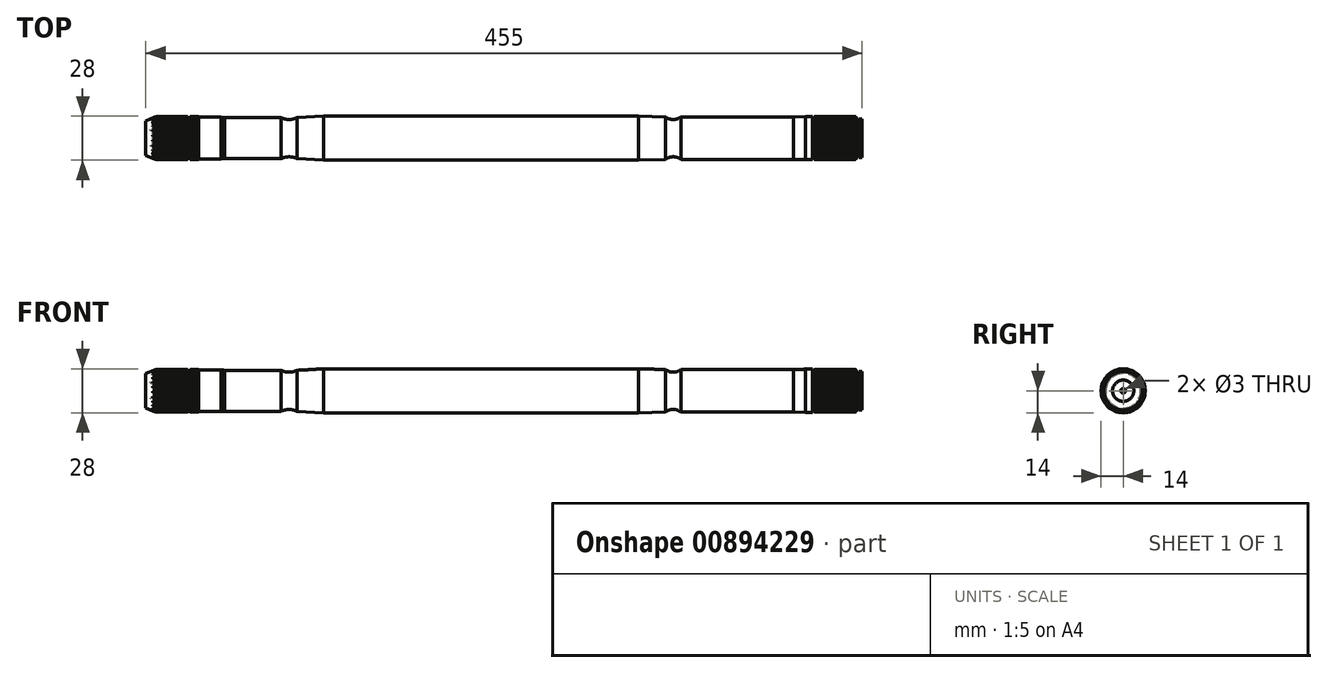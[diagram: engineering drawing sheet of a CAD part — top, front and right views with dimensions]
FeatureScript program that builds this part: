
annotation { "Feature Type Name" : "Feature", "Feature Type Description" : "" }
export const myFeature = defineFeature(function(context is Context, id is Id, definition is map)
    precondition{}
    {
        {
            var Q0;
            Q0=qCreatedBy(makeId("Front.planeOp"),FACE);
            var sketch = newSketch(context, id + "F0", { "sketchPlane" : qUnion([Q0])});
            skLineSegment(sketch, "E0", {"start": v(0, 6.75) * mm, "end": v(0, 12.2) * mm});
            skLineSegment(sketch, "E1.MirrorCS", {"start": v(-31, 12.75) * mm, "end": v(-31.5, 12.75) * mm});
            skLineSegment(sketch, "E2.MirrorCS", {"start": v(-31.5, 13.75) * mm, "end": v(-31.5, 12.75) * mm});
            skLineSegment(sketch, "E3.MirrorCS", {"start": v(-31, 12.75) * mm, "end": v(-30, 13.75) * mm});
            skLineSegment(sketch, "E4.MirrorCS", {"start": v(-31.5, 13.75) * mm, "end": v(-36, 13.75) * mm});
            skLineSegment(sketch, "E5.MirrorCS", {"start": v(-426.7, 13) * mm, "end": v(-428.5, 13) * mm});
            skLineSegment(sketch, "E6.MirrorCS", {"start": v(-421.5, 13.25) * mm, "end": v(-421.5, 13.75) * mm});
            skLineSegment(sketch, "E7.MirrorCS", {"start": v(-428.5, 13.75) * mm, "end": v(-428.5, 13) * mm});
            skLineSegment(sketch, "E8.MirrorCS", {"start": v(-426.7, 13.75) * mm, "end": v(-421.5, 13.75) * mm});
            skLineSegment(sketch, "E9.MirrorCS", {"start": v(-2, 12.2) * mm, "end": v(-2, 11.43) * mm});
            skLineSegment(sketch, "E10.MirrorCS", {"start": v(-426.7, 13.75) * mm, "end": v(-426.7, 13) * mm});
            skLineSegment(sketch, "E11.MirrorCS", {"start": v(-3.5, 11.43) * mm, "end": v(-3.5, 12.75) * mm});
            skLineSegment(sketch, "E12.MirrorCS", {"start": v(-4.5, 13.75) * mm, "end": v(-3.5, 12.75) * mm});
            skLineSegment(sketch, "E13.MirrorCS", {"start": v(0, 12.2) * mm, "end": v(-2, 12.2) * mm});
            skLineSegment(sketch, "E14.MirrorCS", {"start": v(-3.5, 11.43) * mm, "end": v(-2, 11.43) * mm});
            skLineSegment(sketch, "E15.MirrorCS", {"start": v(-443, 0) * mm, "end": v(-443.9, 1.5) * mm});
            skLineSegment(sketch, "E16.MirrorCS", {"start": v(-448, 13.75) * mm, "end": v(-455, 11) * mm});
            skLineSegment(sketch, "E17.MirrorCS", {"start": v(0, 6.75) * mm, "end": v(-9.1, 1.5) * mm});
            skLineSegment(sketch, "E18.MirrorCS", {"start": v(-405, 13) * mm, "end": v(-407, 13.25) * mm});
            skLineSegment(sketch, "E19.MirrorCS", {"start": v(-407, 13.25) * mm, "end": v(-421.5, 13.25) * mm});
            skArc(sketch, "E20.MirrorCS", {"start": v(-115, 13.5) * mm, "mid": v(-120, 11.85) * mm, "end": v(-125, 13.5) * mm});
            skLineSegment(sketch, "E21.MirrorCS", {"start": v(-455, 6.75) * mm, "end": v(-455, 11) * mm});
            skLineSegment(sketch, "E22.MirrorCS", {"start": v(-11.1, 1.5) * mm, "end": v(-9.1, 1.5) * mm});
            skLineSegment(sketch, "E23.MirrorCS", {"start": v(-455, 6.75) * mm, "end": v(-446, 1.5) * mm});
            skLineSegment(sketch, "E24.MirrorCS", {"start": v(-11.1, 1.5) * mm, "end": v(-12, 0) * mm});
            skArc(sketch, "E25.MirrorCS", {"start": v(-359, 13) * mm, "mid": v(-364, 11.85) * mm, "end": v(-369, 13) * mm});
            skLineSegment(sketch, "E26.MirrorCS", {"start": v(-36, 13.75) * mm, "end": v(-43.5, 13.5) * mm});
            skLineSegment(sketch, "E27.MirrorCS", {"start": v(-443.9, 1.5) * mm, "end": v(-446, 1.5) * mm});
            skLineSegment(sketch, "E28.MirrorCS", {"start": v(-428.5, 13.75) * mm, "end": v(-448, 13.75) * mm});
            skLineSegment(sketch, "E29.MirrorCS", {"start": v(-342, 14) * mm, "end": v(-359, 13) * mm});
            skLineSegment(sketch, "E30.MirrorCS", {"start": v(-443, 0) * mm, "end": v(-12, 0) * mm});
            skLineSegment(sketch, "E31.MirrorCS", {"start": v(-125, 13.5) * mm, "end": v(-142, 14) * mm});
            skLineSegment(sketch, "E32.MirrorCS", {"start": v(-369, 13) * mm, "end": v(-405, 13) * mm});
            skLineSegment(sketch, "E33.MirrorCS", {"start": v(-342, 14) * mm, "end": v(-142, 14) * mm});
            skLineSegment(sketch, "E34.MirrorCS", {"start": v(-43.5, 13.5) * mm, "end": v(-115, 13.5) * mm});
            skLineSegment(sketch, "E35.MirrorCS", {"start": v(-4.5, 13.75) * mm, "end": v(-30, 13.75) * mm});
            skSolve(sketch);
        }
        {
            var Q0;
            Q0=makeQuery(id+"F0.imprint","IMPRINT",FACE,{"disambiguationData":[TD([[makeQuery(id+"F0.imprint","IMPRINT",EDGE,{"derivedFrom":sQuery(id+"F0.wireOp",EDGE,"E0")}),1.0]])]});
            var Q1;
            Q1=sQuery(id+"F0.wireOp",EDGE,"E30.MirrorCS");
            revolve(context, id + "F1", {"surfaceOperationType" : NewSurfaceOperationType.NEW, "entities" : qUnion([Q0]), "axis" : qUnion([Q1]), "revolveType" : RevolveType.FULL});
        }
        {
            var Q0;
            Q0=qCreatedBy(makeId("Right.planeOp"),FACE);
            var sketch = newSketch(context, id + "F2", { "sketchPlane" : qUnion([Q0])});
            skArc(sketch, "E36", {"start": v(0.5, 13.56) * mm, "mid": v(0.25, 13.57) * mm, "end": v(0, 13.57) * mm});
            skArc(sketch, "E37", {"start": v(1.6, 12.57) * mm, "mid": v(1.47, 12.59) * mm, "end": v(1.34, 12.6) * mm});
            skLineSegment(sketch, "E38", {"start": v(1.34, 12.6) * mm, "end": v(0.5, 13.56) * mm});
            skArc(sketch, "E39", {"start": v(0, 13.57) * mm, "mid": v(-0.25, 13.57) * mm, "end": v(-0.5, 13.56) * mm});
            skArc(sketch, "E40", {"start": v(-1.34, 12.6) * mm, "mid": v(-1.47, 12.59) * mm, "end": v(-1.6, 12.57) * mm});
            skLineSegment(sketch, "E41", {"start": v(-1.34, 12.6) * mm, "end": v(-0.5, 13.56) * mm});
            skArc(sketch, "E42", {"start": v(-2.9, 13.26) * mm, "mid": v(-3.14, 13.2) * mm, "end": v(-3.38, 13.15) * mm});
            skArc(sketch, "E43", {"start": v(-1.6, 12.57) * mm, "mid": v(-1.72, 12.56) * mm, "end": v(-1.84, 12.54) * mm});
            skLineSegment(sketch, "E44", {"start": v(-1.84, 12.54) * mm, "end": v(-2.9, 13.26) * mm});
            skArc(sketch, "E45", {"start": v(-3.38, 13.15) * mm, "mid": v(-3.62, 13.08) * mm, "end": v(-3.86, 13.01) * mm});
            skArc(sketch, "E46", {"start": v(-4.44, 11.87) * mm, "mid": v(-4.56, 11.83) * mm, "end": v(-4.68, 11.78) * mm});
            skLineSegment(sketch, "E47", {"start": v(-4.44, 11.87) * mm, "end": v(-3.86, 13.01) * mm});
            skArc(sketch, "E48", {"start": v(-6.1, 12.12) * mm, "mid": v(-6.33, 12) * mm, "end": v(-6.55, 11.9) * mm});
            skArc(sketch, "E49", {"start": v(-4.68, 11.78) * mm, "mid": v(-4.8, 11.73) * mm, "end": v(-4.9, 11.69) * mm});
            skLineSegment(sketch, "E50", {"start": v(-4.9, 11.69) * mm, "end": v(-6.1, 12.12) * mm});
            skArc(sketch, "E51", {"start": v(-6.55, 11.9) * mm, "mid": v(-6.77, 11.77) * mm, "end": v(-6.99, 11.64) * mm});
            skArc(sketch, "E52", {"start": v(-7.26, 10.4) * mm, "mid": v(-7.36, 10.32) * mm, "end": v(-7.46, 10.25) * mm});
            skLineSegment(sketch, "E53", {"start": v(-7.26, 10.4) * mm, "end": v(-6.99, 11.64) * mm});
            skArc(sketch, "E54", {"start": v(-8.94, 10.22) * mm, "mid": v(-9.13, 10.06) * mm, "end": v(-9.3, 9.89) * mm});
            skArc(sketch, "E55", {"start": v(-7.46, 10.25) * mm, "mid": v(-7.57, 10.17) * mm, "end": v(-7.67, 10.1) * mm});
            skLineSegment(sketch, "E56", {"start": v(-7.67, 10.1) * mm, "end": v(-8.94, 10.22) * mm});
            skArc(sketch, "E57", {"start": v(-9.3, 9.89) * mm, "mid": v(-9.5, 9.71) * mm, "end": v(-9.67, 9.54) * mm});
            skArc(sketch, "E58", {"start": v(-9.62, 8.26) * mm, "mid": v(-9.7, 8.17) * mm, "end": v(-9.79, 8.07) * mm});
            skLineSegment(sketch, "E59", {"start": v(-9.62, 8.26) * mm, "end": v(-9.67, 9.54) * mm});
            skArc(sketch, "E60", {"start": v(-11.2, 7.68) * mm, "mid": v(-11.35, 7.47) * mm, "end": v(-11.48, 7.26) * mm});
            skArc(sketch, "E61", {"start": v(-9.79, 8.07) * mm, "mid": v(-9.87, 7.97) * mm, "end": v(-9.94, 7.87) * mm});
            skLineSegment(sketch, "E62", {"start": v(-9.94, 7.87) * mm, "end": v(-11.2, 7.68) * mm});
            skArc(sketch, "E63", {"start": v(-11.48, 7.26) * mm, "mid": v(-11.61, 7.05) * mm, "end": v(-11.74, 6.83) * mm});
            skArc(sketch, "E64", {"start": v(-11.38, 5.6) * mm, "mid": v(-11.44, 5.5) * mm, "end": v(-11.5, 5.38) * mm});
            skLineSegment(sketch, "E65", {"start": v(-11.38, 5.6) * mm, "end": v(-11.74, 6.83) * mm});
            skArc(sketch, "E66", {"start": v(-12.77, 4.65) * mm, "mid": v(-12.85, 4.41) * mm, "end": v(-12.93, 4.18) * mm});
            skArc(sketch, "E67", {"start": v(-11.5, 5.38) * mm, "mid": v(-11.54, 5.27) * mm, "end": v(-11.6, 5.15) * mm});
            skLineSegment(sketch, "E68", {"start": v(-11.6, 5.15) * mm, "end": v(-12.77, 4.65) * mm});
            skArc(sketch, "E69", {"start": v(-12.93, 4.18) * mm, "mid": v(-13, 3.94) * mm, "end": v(-13.08, 3.7) * mm});
            skArc(sketch, "E70", {"start": v(-12.43, 2.6) * mm, "mid": v(-12.45, 2.48) * mm, "end": v(-12.48, 2.35) * mm});
            skLineSegment(sketch, "E71", {"start": v(-12.43, 2.6) * mm, "end": v(-13.08, 3.7) * mm});
            skArc(sketch, "E72", {"start": v(-13.53, 1.33) * mm, "mid": v(-13.56, 1.08) * mm, "end": v(-13.57, 0.83) * mm});
            skArc(sketch, "E73", {"start": v(-12.48, 2.35) * mm, "mid": v(-12.5, 2.23) * mm, "end": v(-12.52, 2.1) * mm});
            skLineSegment(sketch, "E74", {"start": v(-12.52, 2.1) * mm, "end": v(-13.53, 1.33) * mm});
            skArc(sketch, "E75", {"start": v(-13.57, 0.83) * mm, "mid": v(-13.59, 0.58) * mm, "end": v(-13.6, 0.33) * mm});
            skArc(sketch, "E76", {"start": v(-12.69, -0.57) * mm, "mid": v(-12.68, -0.7) * mm, "end": v(-12.67, -0.82) * mm});
            skLineSegment(sketch, "E77", {"start": v(-12.69, -0.57) * mm, "end": v(-13.6, 0.33) * mm});
            skArc(sketch, "E78", {"start": v(-13.44, -2.08) * mm, "mid": v(-13.4, -2.33) * mm, "end": v(-13.36, -2.58) * mm});
            skArc(sketch, "E79", {"start": v(-12.67, -0.82) * mm, "mid": v(-12.67, -0.95) * mm, "end": v(-12.66, -1.08) * mm});
            skLineSegment(sketch, "E80", {"start": v(-12.66, -1.08) * mm, "end": v(-13.44, -2.08) * mm});
            skArc(sketch, "E81", {"start": v(-13.36, -2.58) * mm, "mid": v(-13.3, -2.82) * mm, "end": v(-13.26, -3.06) * mm});
            skArc(sketch, "E82", {"start": v(-12.15, -3.71) * mm, "mid": v(-12.12, -3.83) * mm, "end": v(-12.08, -3.95) * mm});
            skLineSegment(sketch, "E83", {"start": v(-12.15, -3.71) * mm, "end": v(-13.26, -3.06) * mm});
            skArc(sketch, "E84", {"start": v(-12.51, -5.36) * mm, "mid": v(-12.41, -5.6) * mm, "end": v(-12.3, -5.82) * mm});
            skArc(sketch, "E85", {"start": v(-12.08, -3.95) * mm, "mid": v(-12.04, -4.07) * mm, "end": v(-12, -4.2) * mm});
            skLineSegment(sketch, "E86", {"start": v(-12, -4.2) * mm, "end": v(-12.51, -5.36) * mm});
            skArc(sketch, "E87", {"start": v(-12.3, -5.82) * mm, "mid": v(-12.2, -6.04) * mm, "end": v(-12.08, -6.27) * mm});
            skArc(sketch, "E88", {"start": v(-10.86, -6.62) * mm, "mid": v(-10.79, -6.73) * mm, "end": v(-10.72, -6.83) * mm});
            skLineSegment(sketch, "E89", {"start": v(-10.86, -6.62) * mm, "end": v(-12.08, -6.27) * mm});
            skArc(sketch, "E90", {"start": v(-10.8, -8.3) * mm, "mid": v(-10.64, -8.5) * mm, "end": v(-10.48, -8.7) * mm});
            skArc(sketch, "E91", {"start": v(-10.72, -6.83) * mm, "mid": v(-10.65, -6.94) * mm, "end": v(-10.59, -7.04) * mm});
            skLineSegment(sketch, "E92", {"start": v(-10.59, -7.04) * mm, "end": v(-10.8, -8.3) * mm});
            skArc(sketch, "E93", {"start": v(-10.48, -8.7) * mm, "mid": v(-10.32, -8.89) * mm, "end": v(-10.15, -9.08) * mm});
            skArc(sketch, "E94", {"start": v(-8.88, -9.11) * mm, "mid": v(-8.79, -9.2) * mm, "end": v(-8.7, -9.28) * mm});
            skLineSegment(sketch, "E95", {"start": v(-8.88, -9.11) * mm, "end": v(-10.15, -9.08) * mm});
            skArc(sketch, "E96", {"start": v(-8.4, -10.73) * mm, "mid": v(-8.2, -10.88) * mm, "end": v(-8, -11.03) * mm});
            skArc(sketch, "E97", {"start": v(-8.7, -9.28) * mm, "mid": v(-8.6, -9.37) * mm, "end": v(-8.5, -9.46) * mm});
            skLineSegment(sketch, "E98", {"start": v(-8.5, -9.46) * mm, "end": v(-8.4, -10.73) * mm});
            skArc(sketch, "E99", {"start": v(-8, -11.03) * mm, "mid": v(-7.8, -11.17) * mm, "end": v(-7.58, -11.32) * mm});
            skArc(sketch, "E100", {"start": v(-6.34, -11.03) * mm, "mid": v(-6.23, -11.1) * mm, "end": v(-6.12, -11.16) * mm});
            skLineSegment(sketch, "E101", {"start": v(-6.34, -11.03) * mm, "end": v(-7.58, -11.32) * mm});
            skArc(sketch, "E102", {"start": v(-5.47, -12.48) * mm, "mid": v(-5.24, -12.58) * mm, "end": v(-5, -12.67) * mm});
            skArc(sketch, "E103", {"start": v(-6.12, -11.16) * mm, "mid": v(-6, -11.22) * mm, "end": v(-5.9, -11.28) * mm});
            skLineSegment(sketch, "E104", {"start": v(-5.9, -11.28) * mm, "end": v(-5.47, -12.48) * mm});
            skArc(sketch, "E105", {"start": v(-5, -12.67) * mm, "mid": v(-4.77, -12.76) * mm, "end": v(-4.54, -12.85) * mm});
            skArc(sketch, "E106", {"start": v(-3.4, -12.26) * mm, "mid": v(-3.28, -12.3) * mm, "end": v(-3.16, -12.33) * mm});
            skLineSegment(sketch, "E107", {"start": v(-3.4, -12.26) * mm, "end": v(-4.54, -12.85) * mm});
            skArc(sketch, "E108", {"start": v(-2.2, -13.45) * mm, "mid": v(-1.95, -13.49) * mm, "end": v(-1.7, -13.52) * mm});
            skArc(sketch, "E109", {"start": v(-3.16, -12.33) * mm, "mid": v(-3.04, -12.36) * mm, "end": v(-2.91, -12.39) * mm});
            skLineSegment(sketch, "E110", {"start": v(-2.91, -12.39) * mm, "end": v(-2.2, -13.45) * mm});
            skArc(sketch, "E111", {"start": v(-1.7, -13.52) * mm, "mid": v(-1.46, -13.55) * mm, "end": v(-1.2, -13.57) * mm});
            skArc(sketch, "E112", {"start": v(-0.25, -12.72) * mm, "mid": v(-0.13, -12.73) * mm, "end": v(0, -12.73) * mm});
            skLineSegment(sketch, "E113", {"start": v(-0.25, -12.72) * mm, "end": v(-1.2, -13.57) * mm});
            skArc(sketch, "E114", {"start": v(1.2, -13.57) * mm, "mid": v(1.46, -13.55) * mm, "end": v(1.7, -13.52) * mm});
            skArc(sketch, "E115", {"start": v(0, -12.73) * mm, "mid": v(0.13, -12.73) * mm, "end": v(0.25, -12.72) * mm});
            skLineSegment(sketch, "E116", {"start": v(0.25, -12.72) * mm, "end": v(1.2, -13.57) * mm});
            skArc(sketch, "E117", {"start": v(1.7, -13.52) * mm, "mid": v(1.95, -13.49) * mm, "end": v(2.2, -13.45) * mm});
            skArc(sketch, "E118", {"start": v(2.91, -12.39) * mm, "mid": v(3.04, -12.36) * mm, "end": v(3.16, -12.33) * mm});
            skLineSegment(sketch, "E119", {"start": v(2.91, -12.39) * mm, "end": v(2.2, -13.45) * mm});
            skArc(sketch, "E120", {"start": v(4.54, -12.85) * mm, "mid": v(4.77, -12.76) * mm, "end": v(5, -12.67) * mm});
            skArc(sketch, "E121", {"start": v(3.16, -12.33) * mm, "mid": v(3.28, -12.3) * mm, "end": v(3.4, -12.26) * mm});
            skLineSegment(sketch, "E122", {"start": v(3.4, -12.26) * mm, "end": v(4.54, -12.85) * mm});
            skArc(sketch, "E123", {"start": v(5, -12.67) * mm, "mid": v(5.24, -12.58) * mm, "end": v(5.47, -12.48) * mm});
            skArc(sketch, "E124", {"start": v(5.9, -11.28) * mm, "mid": v(6, -11.22) * mm, "end": v(6.12, -11.16) * mm});
            skLineSegment(sketch, "E125", {"start": v(5.9, -11.28) * mm, "end": v(5.47, -12.48) * mm});
            skArc(sketch, "E126", {"start": v(7.58, -11.32) * mm, "mid": v(7.8, -11.17) * mm, "end": v(8, -11.03) * mm});
            skArc(sketch, "E127", {"start": v(6.12, -11.16) * mm, "mid": v(6.23, -11.1) * mm, "end": v(6.34, -11.03) * mm});
            skLineSegment(sketch, "E128", {"start": v(6.34, -11.03) * mm, "end": v(7.58, -11.32) * mm});
            skArc(sketch, "E129", {"start": v(8, -11.03) * mm, "mid": v(8.2, -10.88) * mm, "end": v(8.4, -10.73) * mm});
            skArc(sketch, "E130", {"start": v(8.5, -9.46) * mm, "mid": v(8.6, -9.37) * mm, "end": v(8.7, -9.28) * mm});
            skLineSegment(sketch, "E131", {"start": v(8.5, -9.46) * mm, "end": v(8.4, -10.73) * mm});
            skArc(sketch, "E132", {"start": v(10.15, -9.08) * mm, "mid": v(10.32, -8.89) * mm, "end": v(10.48, -8.7) * mm});
            skArc(sketch, "E133", {"start": v(8.7, -9.28) * mm, "mid": v(8.79, -9.2) * mm, "end": v(8.88, -9.11) * mm});
            skLineSegment(sketch, "E134", {"start": v(8.88, -9.11) * mm, "end": v(10.15, -9.08) * mm});
            skArc(sketch, "E135", {"start": v(10.48, -8.7) * mm, "mid": v(10.64, -8.5) * mm, "end": v(10.8, -8.3) * mm});
            skArc(sketch, "E136", {"start": v(10.59, -7.04) * mm, "mid": v(10.65, -6.94) * mm, "end": v(10.72, -6.83) * mm});
            skLineSegment(sketch, "E137", {"start": v(10.59, -7.04) * mm, "end": v(10.8, -8.3) * mm});
            skArc(sketch, "E138", {"start": v(12.08, -6.27) * mm, "mid": v(12.2, -6.04) * mm, "end": v(12.3, -5.82) * mm});
            skArc(sketch, "E139", {"start": v(10.72, -6.83) * mm, "mid": v(10.79, -6.73) * mm, "end": v(10.86, -6.62) * mm});
            skLineSegment(sketch, "E140", {"start": v(10.86, -6.62) * mm, "end": v(12.08, -6.27) * mm});
            skArc(sketch, "E141", {"start": v(12.3, -5.82) * mm, "mid": v(12.41, -5.6) * mm, "end": v(12.51, -5.36) * mm});
            skArc(sketch, "E142", {"start": v(12, -4.2) * mm, "mid": v(12.04, -4.07) * mm, "end": v(12.08, -3.95) * mm});
            skLineSegment(sketch, "E143", {"start": v(12, -4.2) * mm, "end": v(12.51, -5.36) * mm});
            skArc(sketch, "E144", {"start": v(13.26, -3.06) * mm, "mid": v(13.3, -2.82) * mm, "end": v(13.36, -2.58) * mm});
            skArc(sketch, "E145", {"start": v(12.08, -3.95) * mm, "mid": v(12.12, -3.83) * mm, "end": v(12.15, -3.71) * mm});
            skLineSegment(sketch, "E146", {"start": v(12.15, -3.71) * mm, "end": v(13.26, -3.06) * mm});
            skArc(sketch, "E147", {"start": v(13.36, -2.58) * mm, "mid": v(13.4, -2.33) * mm, "end": v(13.44, -2.08) * mm});
            skArc(sketch, "E148", {"start": v(12.66, -1.08) * mm, "mid": v(12.67, -0.95) * mm, "end": v(12.67, -0.82) * mm});
            skLineSegment(sketch, "E149", {"start": v(12.66, -1.08) * mm, "end": v(13.44, -2.08) * mm});
            skArc(sketch, "E150", {"start": v(13.6, 0.33) * mm, "mid": v(13.59, 0.58) * mm, "end": v(13.57, 0.83) * mm});
            skArc(sketch, "E151", {"start": v(12.67, -0.82) * mm, "mid": v(12.68, -0.7) * mm, "end": v(12.69, -0.57) * mm});
            skLineSegment(sketch, "E152", {"start": v(12.69, -0.57) * mm, "end": v(13.6, 0.33) * mm});
            skArc(sketch, "E153", {"start": v(13.57, 0.83) * mm, "mid": v(13.56, 1.08) * mm, "end": v(13.53, 1.33) * mm});
            skArc(sketch, "E154", {"start": v(12.52, 2.1) * mm, "mid": v(12.5, 2.23) * mm, "end": v(12.48, 2.35) * mm});
            skLineSegment(sketch, "E155", {"start": v(12.52, 2.1) * mm, "end": v(13.53, 1.33) * mm});
            skArc(sketch, "E156", {"start": v(13.08, 3.7) * mm, "mid": v(13, 3.94) * mm, "end": v(12.93, 4.18) * mm});
            skArc(sketch, "E157", {"start": v(12.48, 2.35) * mm, "mid": v(12.45, 2.48) * mm, "end": v(12.43, 2.6) * mm});
            skLineSegment(sketch, "E158", {"start": v(12.43, 2.6) * mm, "end": v(13.08, 3.7) * mm});
            skArc(sketch, "E159", {"start": v(12.93, 4.18) * mm, "mid": v(12.85, 4.41) * mm, "end": v(12.77, 4.65) * mm});
            skArc(sketch, "E160", {"start": v(11.6, 5.15) * mm, "mid": v(11.54, 5.27) * mm, "end": v(11.5, 5.38) * mm});
            skLineSegment(sketch, "E161", {"start": v(11.6, 5.15) * mm, "end": v(12.77, 4.65) * mm});
            skArc(sketch, "E162", {"start": v(11.74, 6.83) * mm, "mid": v(11.61, 7.05) * mm, "end": v(11.48, 7.26) * mm});
            skArc(sketch, "E163", {"start": v(11.5, 5.38) * mm, "mid": v(11.44, 5.5) * mm, "end": v(11.38, 5.6) * mm});
            skLineSegment(sketch, "E164", {"start": v(11.38, 5.6) * mm, "end": v(11.74, 6.83) * mm});
            skArc(sketch, "E165", {"start": v(11.48, 7.26) * mm, "mid": v(11.35, 7.47) * mm, "end": v(11.2, 7.68) * mm});
            skArc(sketch, "E166", {"start": v(9.94, 7.87) * mm, "mid": v(9.87, 7.97) * mm, "end": v(9.79, 8.07) * mm});
            skLineSegment(sketch, "E167", {"start": v(9.94, 7.87) * mm, "end": v(11.2, 7.68) * mm});
            skArc(sketch, "E168", {"start": v(9.67, 9.54) * mm, "mid": v(9.5, 9.71) * mm, "end": v(9.3, 9.89) * mm});
            skArc(sketch, "E169", {"start": v(9.79, 8.07) * mm, "mid": v(9.7, 8.17) * mm, "end": v(9.62, 8.26) * mm});
            skLineSegment(sketch, "E170", {"start": v(9.62, 8.26) * mm, "end": v(9.67, 9.54) * mm});
            skArc(sketch, "E171", {"start": v(9.3, 9.89) * mm, "mid": v(9.13, 10.06) * mm, "end": v(8.94, 10.22) * mm});
            skArc(sketch, "E172", {"start": v(7.67, 10.1) * mm, "mid": v(7.57, 10.17) * mm, "end": v(7.46, 10.25) * mm});
            skLineSegment(sketch, "E173", {"start": v(7.67, 10.1) * mm, "end": v(8.94, 10.22) * mm});
            skArc(sketch, "E174", {"start": v(6.99, 11.64) * mm, "mid": v(6.77, 11.77) * mm, "end": v(6.55, 11.9) * mm});
            skArc(sketch, "E175", {"start": v(7.46, 10.25) * mm, "mid": v(7.36, 10.32) * mm, "end": v(7.26, 10.4) * mm});
            skLineSegment(sketch, "E176", {"start": v(7.26, 10.4) * mm, "end": v(6.99, 11.64) * mm});
            skArc(sketch, "E177", {"start": v(6.55, 11.9) * mm, "mid": v(6.33, 12) * mm, "end": v(6.1, 12.12) * mm});
            skArc(sketch, "E178", {"start": v(4.9, 11.69) * mm, "mid": v(4.8, 11.73) * mm, "end": v(4.68, 11.78) * mm});
            skLineSegment(sketch, "E179", {"start": v(4.9, 11.69) * mm, "end": v(6.1, 12.12) * mm});
            skArc(sketch, "E180", {"start": v(3.86, 13.01) * mm, "mid": v(3.62, 13.08) * mm, "end": v(3.38, 13.15) * mm});
            skArc(sketch, "E181", {"start": v(4.68, 11.78) * mm, "mid": v(4.56, 11.83) * mm, "end": v(4.44, 11.87) * mm});
            skLineSegment(sketch, "E182", {"start": v(4.44, 11.87) * mm, "end": v(3.86, 13.01) * mm});
            skArc(sketch, "E183", {"start": v(3.38, 13.15) * mm, "mid": v(3.14, 13.2) * mm, "end": v(2.9, 13.26) * mm});
            skArc(sketch, "E184", {"start": v(1.84, 12.54) * mm, "mid": v(1.72, 12.56) * mm, "end": v(1.6, 12.57) * mm});
            skLineSegment(sketch, "E185", {"start": v(1.84, 12.54) * mm, "end": v(2.9, 13.26) * mm});
            skCircle(sketch, "E186", {"center": v(0, 0) * mm, "radius": 14.27 * mm});
            skSolve(sketch);
        }
        {
            var Q0;
            Q0=qSketchRegion(id+"F2",true);
            var Q1;
            Q1=makeQuery(id+"F1.opRevolve","SWEPT_FACE",FACE,{"disambiguationData":[OSD([sQuery(id+"F0.wireOp",EDGE,"E3.MirrorCS")])]});
            extrude(context, id + "F3", {"entities" : qUnion([Q0]), "operationType" : NewBodyOperationType.REMOVE, "endBound" : BoundingType.UP_TO_SURFACE, "oppositeDirection" : true, "depth" : 25 * mm, "endBoundEntityFace" : qUnion([Q1]), "offsetDistance" : 25 * mm});
        }
        {
            var Q0;
            Q0=makeQuery(id+"F1.opRevolve","SWEPT_FACE",FACE,{"disambiguationData":[OSD([sQuery(id+"F0.wireOp",EDGE,"E21.MirrorCS")])]});
            var sketch = newSketch(context, id + "F4", { "sketchPlane" : qUnion([Q0])});
            skArc(sketch, "E187", {"start": v(0.5, 13.56) * mm, "mid": v(0.25, 13.57) * mm, "end": v(0, 13.57) * mm});
            skArc(sketch, "E188", {"start": v(1.6, 12.57) * mm, "mid": v(1.47, 12.59) * mm, "end": v(1.34, 12.6) * mm});
            skLineSegment(sketch, "E189", {"start": v(1.34, 12.6) * mm, "end": v(0.5, 13.56) * mm});
            skArc(sketch, "E190", {"start": v(0, 13.57) * mm, "mid": v(-0.25, 13.57) * mm, "end": v(-0.5, 13.56) * mm});
            skArc(sketch, "E191", {"start": v(-1.34, 12.6) * mm, "mid": v(-1.47, 12.59) * mm, "end": v(-1.6, 12.57) * mm});
            skLineSegment(sketch, "E192", {"start": v(-1.34, 12.6) * mm, "end": v(-0.5, 13.56) * mm});
            skArc(sketch, "E193", {"start": v(-2.9, 13.26) * mm, "mid": v(-3.14, 13.2) * mm, "end": v(-3.38, 13.15) * mm});
            skArc(sketch, "E194", {"start": v(-1.6, 12.57) * mm, "mid": v(-1.72, 12.56) * mm, "end": v(-1.84, 12.54) * mm});
            skLineSegment(sketch, "E195", {"start": v(-1.84, 12.54) * mm, "end": v(-2.9, 13.26) * mm});
            skArc(sketch, "E196", {"start": v(-3.38, 13.15) * mm, "mid": v(-3.62, 13.08) * mm, "end": v(-3.86, 13.01) * mm});
            skArc(sketch, "E197", {"start": v(-4.44, 11.87) * mm, "mid": v(-4.56, 11.83) * mm, "end": v(-4.68, 11.78) * mm});
            skLineSegment(sketch, "E198", {"start": v(-4.44, 11.87) * mm, "end": v(-3.86, 13.01) * mm});
            skArc(sketch, "E199", {"start": v(-6.1, 12.12) * mm, "mid": v(-6.33, 12) * mm, "end": v(-6.55, 11.9) * mm});
            skArc(sketch, "E200", {"start": v(-4.68, 11.78) * mm, "mid": v(-4.8, 11.73) * mm, "end": v(-4.9, 11.69) * mm});
            skLineSegment(sketch, "E201", {"start": v(-4.9, 11.69) * mm, "end": v(-6.1, 12.12) * mm});
            skArc(sketch, "E202", {"start": v(-6.55, 11.9) * mm, "mid": v(-6.77, 11.77) * mm, "end": v(-6.99, 11.64) * mm});
            skArc(sketch, "E203", {"start": v(-7.26, 10.4) * mm, "mid": v(-7.36, 10.32) * mm, "end": v(-7.46, 10.25) * mm});
            skLineSegment(sketch, "E204", {"start": v(-7.26, 10.4) * mm, "end": v(-6.99, 11.64) * mm});
            skArc(sketch, "E205", {"start": v(-8.94, 10.22) * mm, "mid": v(-9.13, 10.06) * mm, "end": v(-9.3, 9.89) * mm});
            skArc(sketch, "E206", {"start": v(-7.46, 10.25) * mm, "mid": v(-7.57, 10.17) * mm, "end": v(-7.67, 10.1) * mm});
            skLineSegment(sketch, "E207", {"start": v(-7.67, 10.1) * mm, "end": v(-8.94, 10.22) * mm});
            skArc(sketch, "E208", {"start": v(-9.3, 9.89) * mm, "mid": v(-9.5, 9.71) * mm, "end": v(-9.67, 9.54) * mm});
            skArc(sketch, "E209", {"start": v(-9.62, 8.26) * mm, "mid": v(-9.7, 8.17) * mm, "end": v(-9.79, 8.07) * mm});
            skLineSegment(sketch, "E210", {"start": v(-9.62, 8.26) * mm, "end": v(-9.67, 9.54) * mm});
            skArc(sketch, "E211", {"start": v(-11.2, 7.68) * mm, "mid": v(-11.35, 7.47) * mm, "end": v(-11.48, 7.26) * mm});
            skArc(sketch, "E212", {"start": v(-9.79, 8.07) * mm, "mid": v(-9.87, 7.97) * mm, "end": v(-9.94, 7.87) * mm});
            skLineSegment(sketch, "E213", {"start": v(-9.94, 7.87) * mm, "end": v(-11.2, 7.68) * mm});
            skArc(sketch, "E214", {"start": v(-11.48, 7.26) * mm, "mid": v(-11.61, 7.05) * mm, "end": v(-11.74, 6.83) * mm});
            skArc(sketch, "E215", {"start": v(-11.38, 5.6) * mm, "mid": v(-11.44, 5.5) * mm, "end": v(-11.5, 5.38) * mm});
            skLineSegment(sketch, "E216", {"start": v(-11.38, 5.6) * mm, "end": v(-11.74, 6.83) * mm});
            skArc(sketch, "E217", {"start": v(-12.77, 4.65) * mm, "mid": v(-12.85, 4.41) * mm, "end": v(-12.93, 4.18) * mm});
            skArc(sketch, "E218", {"start": v(-11.5, 5.38) * mm, "mid": v(-11.54, 5.27) * mm, "end": v(-11.6, 5.15) * mm});
            skLineSegment(sketch, "E219", {"start": v(-11.6, 5.15) * mm, "end": v(-12.77, 4.65) * mm});
            skArc(sketch, "E220", {"start": v(-12.93, 4.18) * mm, "mid": v(-13, 3.94) * mm, "end": v(-13.08, 3.7) * mm});
            skArc(sketch, "E221", {"start": v(-12.43, 2.6) * mm, "mid": v(-12.45, 2.48) * mm, "end": v(-12.48, 2.35) * mm});
            skLineSegment(sketch, "E222", {"start": v(-12.43, 2.6) * mm, "end": v(-13.08, 3.7) * mm});
            skArc(sketch, "E223", {"start": v(-13.53, 1.33) * mm, "mid": v(-13.56, 1.08) * mm, "end": v(-13.57, 0.83) * mm});
            skArc(sketch, "E224", {"start": v(-12.48, 2.35) * mm, "mid": v(-12.5, 2.23) * mm, "end": v(-12.52, 2.1) * mm});
            skLineSegment(sketch, "E225", {"start": v(-12.52, 2.1) * mm, "end": v(-13.53, 1.33) * mm});
            skArc(sketch, "E226", {"start": v(-13.57, 0.83) * mm, "mid": v(-13.59, 0.58) * mm, "end": v(-13.6, 0.33) * mm});
            skArc(sketch, "E227", {"start": v(-12.69, -0.57) * mm, "mid": v(-12.68, -0.7) * mm, "end": v(-12.67, -0.82) * mm});
            skLineSegment(sketch, "E228", {"start": v(-12.69, -0.57) * mm, "end": v(-13.6, 0.33) * mm});
            skArc(sketch, "E229", {"start": v(-13.44, -2.08) * mm, "mid": v(-13.4, -2.33) * mm, "end": v(-13.36, -2.58) * mm});
            skArc(sketch, "E230", {"start": v(-12.67, -0.82) * mm, "mid": v(-12.67, -0.95) * mm, "end": v(-12.66, -1.08) * mm});
            skLineSegment(sketch, "E231", {"start": v(-12.66, -1.08) * mm, "end": v(-13.44, -2.08) * mm});
            skArc(sketch, "E232", {"start": v(-13.36, -2.58) * mm, "mid": v(-13.3, -2.82) * mm, "end": v(-13.26, -3.06) * mm});
            skArc(sketch, "E233", {"start": v(-12.15, -3.71) * mm, "mid": v(-12.12, -3.83) * mm, "end": v(-12.08, -3.95) * mm});
            skLineSegment(sketch, "E234", {"start": v(-12.15, -3.71) * mm, "end": v(-13.26, -3.06) * mm});
            skArc(sketch, "E235", {"start": v(-12.51, -5.36) * mm, "mid": v(-12.41, -5.6) * mm, "end": v(-12.3, -5.82) * mm});
            skArc(sketch, "E236", {"start": v(-12.08, -3.95) * mm, "mid": v(-12.04, -4.07) * mm, "end": v(-12, -4.2) * mm});
            skLineSegment(sketch, "E237", {"start": v(-12, -4.2) * mm, "end": v(-12.51, -5.36) * mm});
            skArc(sketch, "E238", {"start": v(-12.3, -5.82) * mm, "mid": v(-12.2, -6.04) * mm, "end": v(-12.08, -6.27) * mm});
            skArc(sketch, "E239", {"start": v(-10.86, -6.62) * mm, "mid": v(-10.79, -6.73) * mm, "end": v(-10.72, -6.83) * mm});
            skLineSegment(sketch, "E240", {"start": v(-10.86, -6.62) * mm, "end": v(-12.08, -6.27) * mm});
            skArc(sketch, "E241", {"start": v(-10.8, -8.3) * mm, "mid": v(-10.64, -8.5) * mm, "end": v(-10.48, -8.7) * mm});
            skArc(sketch, "E242", {"start": v(-10.72, -6.83) * mm, "mid": v(-10.65, -6.94) * mm, "end": v(-10.59, -7.04) * mm});
            skLineSegment(sketch, "E243", {"start": v(-10.59, -7.04) * mm, "end": v(-10.8, -8.3) * mm});
            skArc(sketch, "E244", {"start": v(-10.48, -8.7) * mm, "mid": v(-10.32, -8.89) * mm, "end": v(-10.15, -9.08) * mm});
            skArc(sketch, "E245", {"start": v(-8.88, -9.11) * mm, "mid": v(-8.79, -9.2) * mm, "end": v(-8.7, -9.28) * mm});
            skLineSegment(sketch, "E246", {"start": v(-8.88, -9.11) * mm, "end": v(-10.15, -9.08) * mm});
            skArc(sketch, "E247", {"start": v(-8.4, -10.73) * mm, "mid": v(-8.2, -10.88) * mm, "end": v(-8, -11.03) * mm});
            skArc(sketch, "E248", {"start": v(-8.7, -9.28) * mm, "mid": v(-8.6, -9.37) * mm, "end": v(-8.5, -9.46) * mm});
            skLineSegment(sketch, "E249", {"start": v(-8.5, -9.46) * mm, "end": v(-8.4, -10.73) * mm});
            skArc(sketch, "E250", {"start": v(-8, -11.03) * mm, "mid": v(-7.8, -11.17) * mm, "end": v(-7.58, -11.32) * mm});
            skArc(sketch, "E251", {"start": v(-6.34, -11.03) * mm, "mid": v(-6.23, -11.1) * mm, "end": v(-6.12, -11.16) * mm});
            skLineSegment(sketch, "E252", {"start": v(-6.34, -11.03) * mm, "end": v(-7.58, -11.32) * mm});
            skArc(sketch, "E253", {"start": v(-5.47, -12.48) * mm, "mid": v(-5.24, -12.58) * mm, "end": v(-5, -12.67) * mm});
            skArc(sketch, "E254", {"start": v(-6.12, -11.16) * mm, "mid": v(-6, -11.22) * mm, "end": v(-5.9, -11.28) * mm});
            skLineSegment(sketch, "E255", {"start": v(-5.9, -11.28) * mm, "end": v(-5.47, -12.48) * mm});
            skArc(sketch, "E256", {"start": v(-5, -12.67) * mm, "mid": v(-4.77, -12.76) * mm, "end": v(-4.54, -12.85) * mm});
            skArc(sketch, "E257", {"start": v(-3.4, -12.26) * mm, "mid": v(-3.28, -12.3) * mm, "end": v(-3.16, -12.33) * mm});
            skLineSegment(sketch, "E258", {"start": v(-3.4, -12.26) * mm, "end": v(-4.54, -12.85) * mm});
            skArc(sketch, "E259", {"start": v(-2.2, -13.45) * mm, "mid": v(-1.95, -13.49) * mm, "end": v(-1.7, -13.52) * mm});
            skArc(sketch, "E260", {"start": v(-3.16, -12.33) * mm, "mid": v(-3.04, -12.36) * mm, "end": v(-2.91, -12.39) * mm});
            skLineSegment(sketch, "E261", {"start": v(-2.91, -12.39) * mm, "end": v(-2.2, -13.45) * mm});
            skArc(sketch, "E262", {"start": v(-1.7, -13.52) * mm, "mid": v(-1.46, -13.55) * mm, "end": v(-1.2, -13.57) * mm});
            skArc(sketch, "E263", {"start": v(-0.25, -12.72) * mm, "mid": v(-0.13, -12.73) * mm, "end": v(0, -12.73) * mm});
            skLineSegment(sketch, "E264", {"start": v(-0.25, -12.72) * mm, "end": v(-1.2, -13.57) * mm});
            skArc(sketch, "E265", {"start": v(1.2, -13.57) * mm, "mid": v(1.46, -13.55) * mm, "end": v(1.7, -13.52) * mm});
            skArc(sketch, "E266", {"start": v(0, -12.73) * mm, "mid": v(0.13, -12.73) * mm, "end": v(0.25, -12.72) * mm});
            skLineSegment(sketch, "E267", {"start": v(0.25, -12.72) * mm, "end": v(1.2, -13.57) * mm});
            skArc(sketch, "E268", {"start": v(1.7, -13.52) * mm, "mid": v(1.95, -13.49) * mm, "end": v(2.2, -13.45) * mm});
            skArc(sketch, "E269", {"start": v(2.91, -12.39) * mm, "mid": v(3.04, -12.36) * mm, "end": v(3.16, -12.33) * mm});
            skLineSegment(sketch, "E270", {"start": v(2.91, -12.39) * mm, "end": v(2.2, -13.45) * mm});
            skArc(sketch, "E271", {"start": v(4.54, -12.85) * mm, "mid": v(4.77, -12.76) * mm, "end": v(5, -12.67) * mm});
            skArc(sketch, "E272", {"start": v(3.16, -12.33) * mm, "mid": v(3.28, -12.3) * mm, "end": v(3.4, -12.26) * mm});
            skLineSegment(sketch, "E273", {"start": v(3.4, -12.26) * mm, "end": v(4.54, -12.85) * mm});
            skArc(sketch, "E274", {"start": v(5, -12.67) * mm, "mid": v(5.24, -12.58) * mm, "end": v(5.47, -12.48) * mm});
            skArc(sketch, "E275", {"start": v(5.9, -11.28) * mm, "mid": v(6, -11.22) * mm, "end": v(6.12, -11.16) * mm});
            skLineSegment(sketch, "E276", {"start": v(5.9, -11.28) * mm, "end": v(5.47, -12.48) * mm});
            skArc(sketch, "E277", {"start": v(7.58, -11.32) * mm, "mid": v(7.8, -11.17) * mm, "end": v(8, -11.03) * mm});
            skArc(sketch, "E278", {"start": v(6.12, -11.16) * mm, "mid": v(6.23, -11.1) * mm, "end": v(6.34, -11.03) * mm});
            skLineSegment(sketch, "E279", {"start": v(6.34, -11.03) * mm, "end": v(7.58, -11.32) * mm});
            skArc(sketch, "E280", {"start": v(8, -11.03) * mm, "mid": v(8.2, -10.88) * mm, "end": v(8.4, -10.73) * mm});
            skArc(sketch, "E281", {"start": v(8.5, -9.46) * mm, "mid": v(8.6, -9.37) * mm, "end": v(8.7, -9.28) * mm});
            skLineSegment(sketch, "E282", {"start": v(8.5, -9.46) * mm, "end": v(8.4, -10.73) * mm});
            skArc(sketch, "E283", {"start": v(10.15, -9.08) * mm, "mid": v(10.32, -8.89) * mm, "end": v(10.48, -8.7) * mm});
            skArc(sketch, "E284", {"start": v(8.7, -9.28) * mm, "mid": v(8.79, -9.2) * mm, "end": v(8.88, -9.11) * mm});
            skLineSegment(sketch, "E285", {"start": v(8.88, -9.11) * mm, "end": v(10.15, -9.08) * mm});
            skArc(sketch, "E286", {"start": v(10.48, -8.7) * mm, "mid": v(10.64, -8.5) * mm, "end": v(10.8, -8.3) * mm});
            skArc(sketch, "E287", {"start": v(10.59, -7.04) * mm, "mid": v(10.65, -6.94) * mm, "end": v(10.72, -6.83) * mm});
            skLineSegment(sketch, "E288", {"start": v(10.59, -7.04) * mm, "end": v(10.8, -8.3) * mm});
            skArc(sketch, "E289", {"start": v(12.08, -6.27) * mm, "mid": v(12.2, -6.04) * mm, "end": v(12.3, -5.82) * mm});
            skArc(sketch, "E290", {"start": v(10.72, -6.83) * mm, "mid": v(10.79, -6.73) * mm, "end": v(10.86, -6.62) * mm});
            skLineSegment(sketch, "E291", {"start": v(10.86, -6.62) * mm, "end": v(12.08, -6.27) * mm});
            skArc(sketch, "E292", {"start": v(12.3, -5.82) * mm, "mid": v(12.41, -5.6) * mm, "end": v(12.51, -5.36) * mm});
            skArc(sketch, "E293", {"start": v(12, -4.2) * mm, "mid": v(12.04, -4.07) * mm, "end": v(12.08, -3.95) * mm});
            skLineSegment(sketch, "E294", {"start": v(12, -4.2) * mm, "end": v(12.51, -5.36) * mm});
            skArc(sketch, "E295", {"start": v(13.26, -3.06) * mm, "mid": v(13.3, -2.82) * mm, "end": v(13.36, -2.58) * mm});
            skArc(sketch, "E296", {"start": v(12.08, -3.95) * mm, "mid": v(12.12, -3.83) * mm, "end": v(12.15, -3.71) * mm});
            skLineSegment(sketch, "E297", {"start": v(12.15, -3.71) * mm, "end": v(13.26, -3.06) * mm});
            skArc(sketch, "E298", {"start": v(13.36, -2.58) * mm, "mid": v(13.4, -2.33) * mm, "end": v(13.44, -2.08) * mm});
            skArc(sketch, "E299", {"start": v(12.66, -1.08) * mm, "mid": v(12.67, -0.95) * mm, "end": v(12.67, -0.82) * mm});
            skLineSegment(sketch, "E300", {"start": v(12.66, -1.08) * mm, "end": v(13.44, -2.08) * mm});
            skArc(sketch, "E301", {"start": v(13.6, 0.33) * mm, "mid": v(13.59, 0.58) * mm, "end": v(13.57, 0.83) * mm});
            skArc(sketch, "E302", {"start": v(12.67, -0.82) * mm, "mid": v(12.68, -0.7) * mm, "end": v(12.69, -0.57) * mm});
            skLineSegment(sketch, "E303", {"start": v(12.69, -0.57) * mm, "end": v(13.6, 0.33) * mm});
            skArc(sketch, "E304", {"start": v(13.57, 0.83) * mm, "mid": v(13.56, 1.08) * mm, "end": v(13.53, 1.33) * mm});
            skArc(sketch, "E305", {"start": v(12.52, 2.1) * mm, "mid": v(12.5, 2.23) * mm, "end": v(12.48, 2.35) * mm});
            skLineSegment(sketch, "E306", {"start": v(12.52, 2.1) * mm, "end": v(13.53, 1.33) * mm});
            skArc(sketch, "E307", {"start": v(13.08, 3.7) * mm, "mid": v(13, 3.94) * mm, "end": v(12.93, 4.18) * mm});
            skArc(sketch, "E308", {"start": v(12.48, 2.35) * mm, "mid": v(12.45, 2.48) * mm, "end": v(12.43, 2.6) * mm});
            skLineSegment(sketch, "E309", {"start": v(12.43, 2.6) * mm, "end": v(13.08, 3.7) * mm});
            skArc(sketch, "E310", {"start": v(12.93, 4.18) * mm, "mid": v(12.85, 4.41) * mm, "end": v(12.77, 4.65) * mm});
            skArc(sketch, "E311", {"start": v(11.6, 5.15) * mm, "mid": v(11.54, 5.27) * mm, "end": v(11.5, 5.38) * mm});
            skLineSegment(sketch, "E312", {"start": v(11.6, 5.15) * mm, "end": v(12.77, 4.65) * mm});
            skArc(sketch, "E313", {"start": v(11.74, 6.83) * mm, "mid": v(11.61, 7.05) * mm, "end": v(11.48, 7.26) * mm});
            skArc(sketch, "E314", {"start": v(11.5, 5.38) * mm, "mid": v(11.44, 5.5) * mm, "end": v(11.38, 5.6) * mm});
            skLineSegment(sketch, "E315", {"start": v(11.38, 5.6) * mm, "end": v(11.74, 6.83) * mm});
            skArc(sketch, "E316", {"start": v(11.48, 7.26) * mm, "mid": v(11.35, 7.47) * mm, "end": v(11.2, 7.68) * mm});
            skArc(sketch, "E317", {"start": v(9.94, 7.87) * mm, "mid": v(9.87, 7.97) * mm, "end": v(9.79, 8.07) * mm});
            skLineSegment(sketch, "E318", {"start": v(9.94, 7.87) * mm, "end": v(11.2, 7.68) * mm});
            skArc(sketch, "E319", {"start": v(9.67, 9.54) * mm, "mid": v(9.5, 9.71) * mm, "end": v(9.3, 9.89) * mm});
            skArc(sketch, "E320", {"start": v(9.79, 8.07) * mm, "mid": v(9.7, 8.17) * mm, "end": v(9.62, 8.26) * mm});
            skLineSegment(sketch, "E321", {"start": v(9.62, 8.26) * mm, "end": v(9.67, 9.54) * mm});
            skArc(sketch, "E322", {"start": v(9.3, 9.89) * mm, "mid": v(9.13, 10.06) * mm, "end": v(8.94, 10.22) * mm});
            skArc(sketch, "E323", {"start": v(7.67, 10.1) * mm, "mid": v(7.57, 10.17) * mm, "end": v(7.46, 10.25) * mm});
            skLineSegment(sketch, "E324", {"start": v(7.67, 10.1) * mm, "end": v(8.94, 10.22) * mm});
            skArc(sketch, "E325", {"start": v(6.99, 11.64) * mm, "mid": v(6.77, 11.77) * mm, "end": v(6.55, 11.9) * mm});
            skArc(sketch, "E326", {"start": v(7.46, 10.25) * mm, "mid": v(7.36, 10.32) * mm, "end": v(7.26, 10.4) * mm});
            skLineSegment(sketch, "E327", {"start": v(7.26, 10.4) * mm, "end": v(6.99, 11.64) * mm});
            skArc(sketch, "E328", {"start": v(6.55, 11.9) * mm, "mid": v(6.33, 12) * mm, "end": v(6.1, 12.12) * mm});
            skArc(sketch, "E329", {"start": v(4.9, 11.69) * mm, "mid": v(4.8, 11.73) * mm, "end": v(4.68, 11.78) * mm});
            skLineSegment(sketch, "E330", {"start": v(4.9, 11.69) * mm, "end": v(6.1, 12.12) * mm});
            skArc(sketch, "E331", {"start": v(3.86, 13.01) * mm, "mid": v(3.62, 13.08) * mm, "end": v(3.38, 13.15) * mm});
            skArc(sketch, "E332", {"start": v(4.68, 11.78) * mm, "mid": v(4.56, 11.83) * mm, "end": v(4.44, 11.87) * mm});
            skLineSegment(sketch, "E333", {"start": v(4.44, 11.87) * mm, "end": v(3.86, 13.01) * mm});
            skArc(sketch, "E334", {"start": v(3.38, 13.15) * mm, "mid": v(3.14, 13.2) * mm, "end": v(2.9, 13.26) * mm});
            skArc(sketch, "E335", {"start": v(1.84, 12.54) * mm, "mid": v(1.72, 12.56) * mm, "end": v(1.6, 12.57) * mm});
            skLineSegment(sketch, "E336", {"start": v(1.84, 12.54) * mm, "end": v(2.9, 13.26) * mm});
            skCircle(sketch, "E337", {"center": v(0, 0) * mm, "radius": 14.51 * mm});
            skSolve(sketch);
        }
        {
            var Q0;
            Q0=qSketchRegion(id+"F4",true);
            var Q1;
            Q1=makeQuery(id+"F1.opRevolve","SWEPT_FACE",FACE,{"disambiguationData":[OSD([sQuery(id+"F0.wireOp",EDGE,"E6.MirrorCS")])]});
            extrude(context, id + "F5", {"entities" : qUnion([Q0]), "operationType" : NewBodyOperationType.REMOVE, "endBound" : BoundingType.UP_TO_SURFACE, "oppositeDirection" : true, "depth" : 25 * mm, "endBoundEntityFace" : qUnion([Q1]), "offsetDistance" : 25 * mm});
        }
    });
